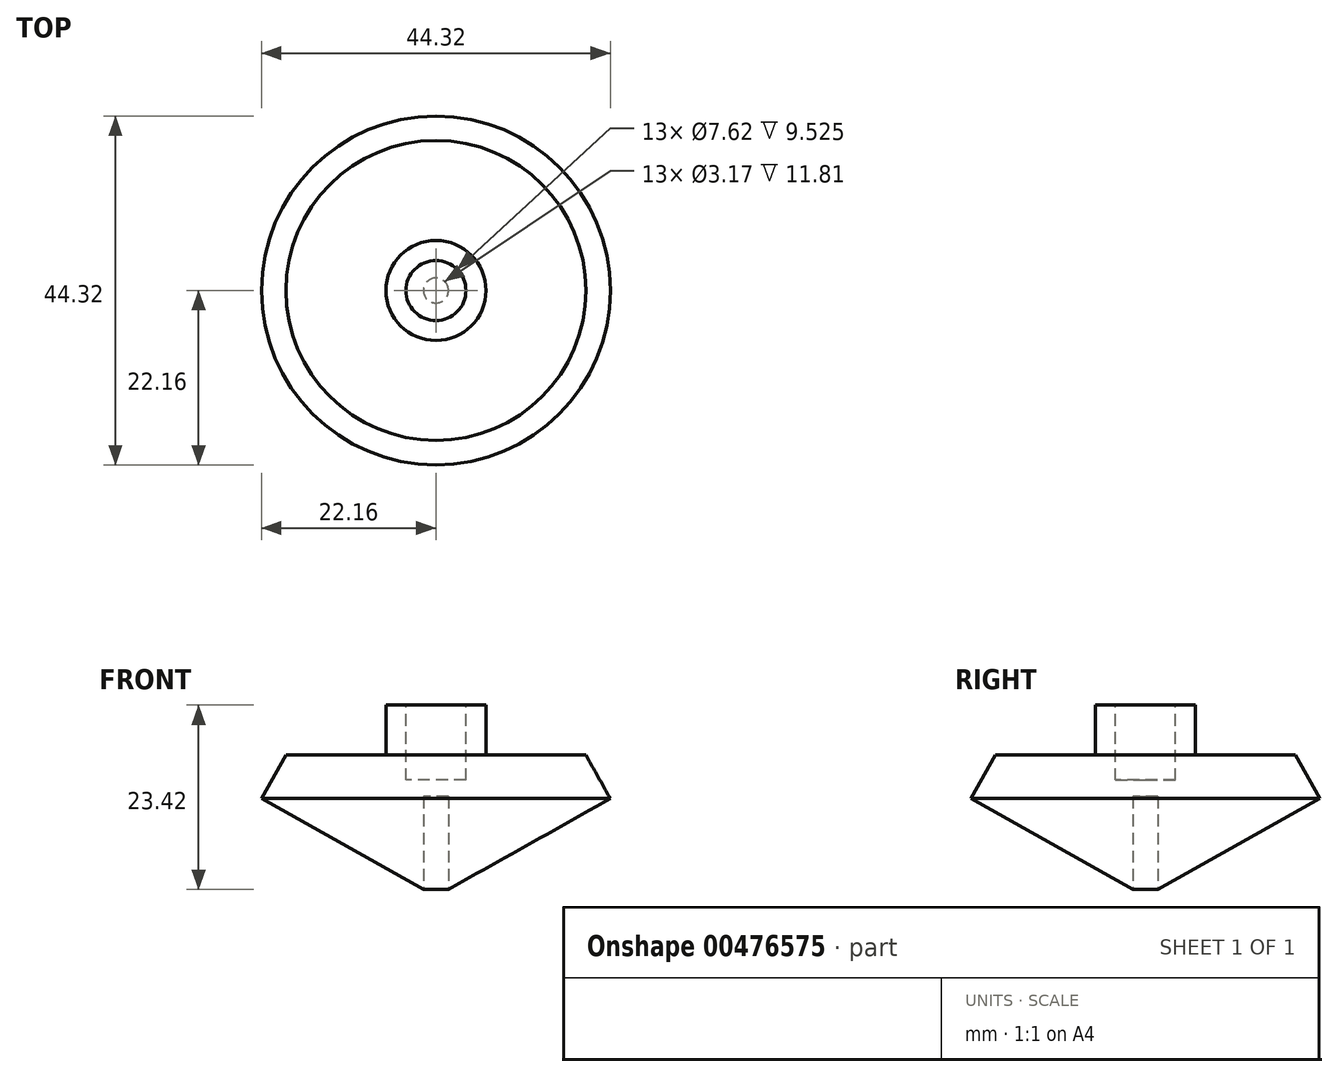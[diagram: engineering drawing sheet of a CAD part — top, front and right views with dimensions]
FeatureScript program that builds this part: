
annotation { "Feature Type Name" : "Feature", "Feature Type Description" : "" }
export const myFeature = defineFeature(function(context is Context, id is Id, definition is map)
    precondition{}
    {
        {
            var Q0;
            Q0=qCreatedBy(makeId("Front.planeOp"),FACE);
            var sketch = newSketch(context, id + "F0", { "sketchPlane" : qUnion([Q0])});
            skLineSegment(sketch, "E0", {"start": v(0, 0) * mm, "end": v(22.16, 12.42) * mm});
            skLineSegment(sketch, "E1", {"start": v(22.16, 12.42) * mm, "end": v(19.05, 17.96) * mm});
            skLineSegment(sketch, "E2", {"start": v(19.05, 17.96) * mm, "end": v(6.35, 17.96) * mm});
            skLineSegment(sketch, "E3", {"start": v(6.35, 17.96) * mm, "end": v(6.35, 24.31) * mm});
            skLineSegment(sketch, "E4", {"start": v(6.35, 24.31) * mm, "end": v(0, 24.31) * mm});
            skLineSegment(sketch, "E5", {"start": v(0, 24.31) * mm, "end": v(0, 0) * mm});
            skSolve(sketch);
        }
        {
            var Q0;
            Q0 = qSketchRegion(id + "F0", true);
            var Q1;
            Q1=sQuery(id+"F0.wireOp",EDGE,"E5");
            revolve(context, id + "F1", {"entities" : qUnion([Q0]), "axis" : qUnion([Q1]), "revolveType" : RevolveType.FULL});
        }
        {
            var Q0;
            Q0=makeQuery(id+"F1.opRevolve","SWEPT_FACE",FACE,{"disambiguationData":[OSD([sQuery(id+"F0.wireOp",EDGE,"E4")])]});
            var sketch = newSketch(context, id + "F2", { "sketchPlane" : qUnion([Q0])});
            skCircle(sketch, "E6", {"center": v(0, 0) * mm, "radius": 3.81 * mm});
            skSolve(sketch);
        }
        {
            var Q0;
            Q0 = qSketchRegion(id + "F2", true);
            extrude(context, id + "F3", {"entities" : qUnion([Q0]), "operationType" : NewBodyOperationType.REMOVE, "oppositeDirection" : true, "depth" : 9.52 * mm});
        }
        {
            var Q0;
            Q0=qCreatedBy(makeId("Top.planeOp"),FACE);
            var sketch = newSketch(context, id + "F4", { "sketchPlane" : qUnion([Q0])});
            skCircle(sketch, "E7", {"center": v(0, 0) * mm, "radius": 1.59 * mm});
            skSolve(sketch);
        }
        {
            var Q0;
            Q0=makeQuery(id+"F4.imprint","IMPRINT",FACE,{"disambiguationData":[TD([[makeQuery(id+"F4.imprint","IMPRINT",EDGE,{"derivedFrom":sQuery(id+"F4.wireOp",EDGE,"E7")}),1.0]])]});
            extrude(context, id + "F5", {"entities" : qUnion([Q0]), "operationType" : NewBodyOperationType.REMOVE, "depth" : 12.7 * mm});
        }
    });
